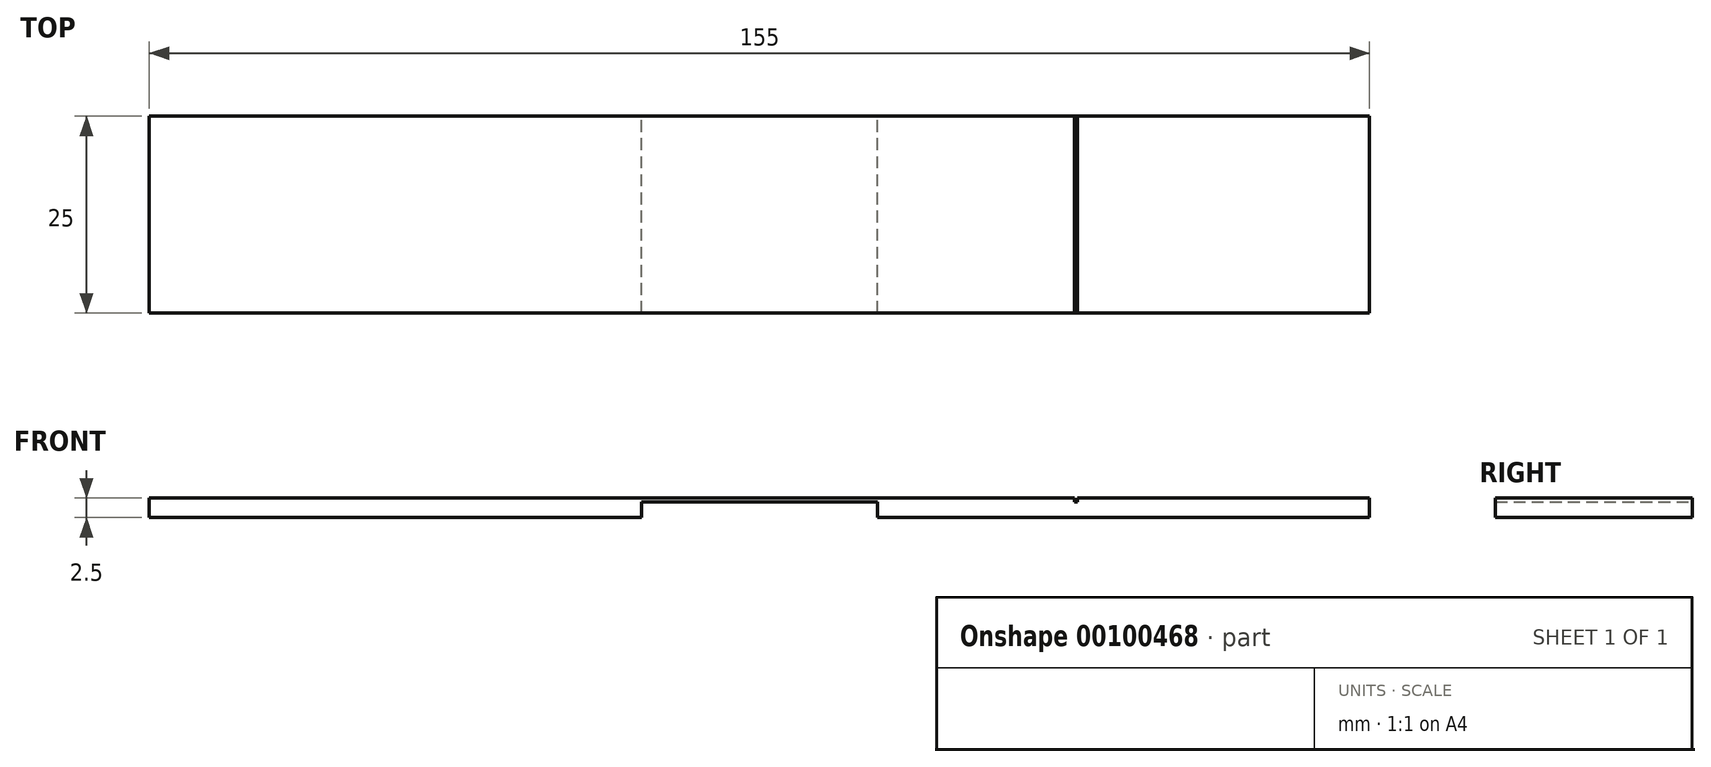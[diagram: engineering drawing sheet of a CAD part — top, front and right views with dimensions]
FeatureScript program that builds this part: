
annotation { "Feature Type Name" : "Feature", "Feature Type Description" : "" }
export const myFeature = defineFeature(function(context is Context, id is Id, definition is map)
    precondition{}
    {
        {
            var Q0;
            Q0=qCreatedBy(makeId("Front.planeOp"),FACE);
            var sketch = newSketch(context, id + "F0", { "sketchPlane" : qUnion([Q0])});
            skLineSegment(sketch, "E0", {"start": v(-77.5, 0) * mm, "end": v(77.5, 0) * mm});
            skLineSegment(sketch, "E1", {"start": v(77.5, 0) * mm, "end": v(77.5, -2.5) * mm});
            skLineSegment(sketch, "E2", {"start": v(77.5, -2.5) * mm, "end": v(15, -2.5) * mm});
            skLineSegment(sketch, "E3", {"start": v(15, -2.5) * mm, "end": v(15, -0.5) * mm});
            skLineSegment(sketch, "E4", {"start": v(15, -0.5) * mm, "end": v(-15, -0.5) * mm});
            skLineSegment(sketch, "E5", {"start": v(-15, -0.5) * mm, "end": v(-15, -2.5) * mm});
            skLineSegment(sketch, "E6", {"start": v(-15, -2.5) * mm, "end": v(-77.5, -2.5) * mm});
            skLineSegment(sketch, "E7", {"start": v(-77.5, -2.5) * mm, "end": v(-77.5, 0) * mm});
            skPoint(sketch, "E8", {"position": v(0, -0.5) * mm});
            skSolve(sketch);
        }
        {
            var Q0;
            Q0 = qSketchRegion(id + "F0", true);
            extrude(context, id + "F1", {"entities" : qUnion([Q0]), "depth" : 25 * mm});
        }
        {
            var Q0;
            Q0=makeQuery(id+"F1.opExtrude","SWEPT_FACE",FACE,{"disambiguationData":[OSD([sQuery(id+"F0.wireOp",EDGE,"E0")])]});
            var sketch = newSketch(context, id + "F2", { "sketchPlane" : qUnion([Q0])});
            skLineSegment(sketch, "E9.bottom", {"start": v(40, 0) * mm, "end": v(40.4, 0) * mm});
            skLineSegment(sketch, "E9.top", {"start": v(40, -25) * mm, "end": v(40.4, -25) * mm});
            skLineSegment(sketch, "E9.left", {"start": v(40, 0) * mm, "end": v(40, -25) * mm});
            skLineSegment(sketch, "E9.right", {"start": v(40.4, 0) * mm, "end": v(40.4, -25) * mm});
            skSolve(sketch);
        }
        {
            var Q0;
            Q0=makeQuery(id+"F2.imprint","IMPRINT",FACE,{"disambiguationData":[TD([[makeQuery(id+"F2.imprint","IMPRINT",EDGE,{"derivedFrom":sQuery(id+"F2.wireOp",EDGE,"E9.bottom")}),-1.0]])]});
            var Q1;
            Q1=makeQuery(id+"F1.opExtrude","SWEPT_FACE",FACE,{"disambiguationData":[OSD([sQuery(id+"F0.wireOp",EDGE,"E4")])]});
            extrude(context, id + "F3", {"entities" : qUnion([Q0]), "operationType" : NewBodyOperationType.REMOVE, "endBound" : BoundingType.UP_TO_SURFACE, "oppositeDirection" : true, "endBoundEntityFace" : qUnion([Q1]), "depth" : .4 * mm});
        }
    });
